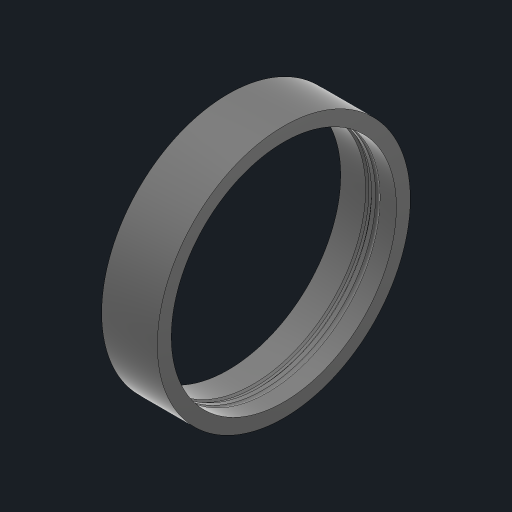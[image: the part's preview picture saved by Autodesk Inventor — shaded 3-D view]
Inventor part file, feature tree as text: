
AUTODESK INVENTOR PART (.ipt)
format: ipt  version: 2023.2 (Build 272271030, 271C)  size: 145,408 bytes
history: native  units: mm
features: revolve x1, sketch x1
ambient origin geometry x8: Origin, YZ Plane, XZ Plane, XY Plane, X Axis, Y Axis, Z Axis, Center Point
bodies: Solid1 (feature_tree)
feature tree (2):
  revolve  "Revolution1"  [1 undecoded]
  sketch  "Sketch1"  dims[d0=2.5mm d1=67.25mm d2=0.5mm d3=75.0mm d4=1.0mm d5=33.0mm d7=4.0mm d8=1.75mm d9=90.0deg]
note: 1 required parameter value undecoded (feature->parameter linkage not recoverable at this tier; creation-order binding heuristic only, values carry confidence <= 0.55)
